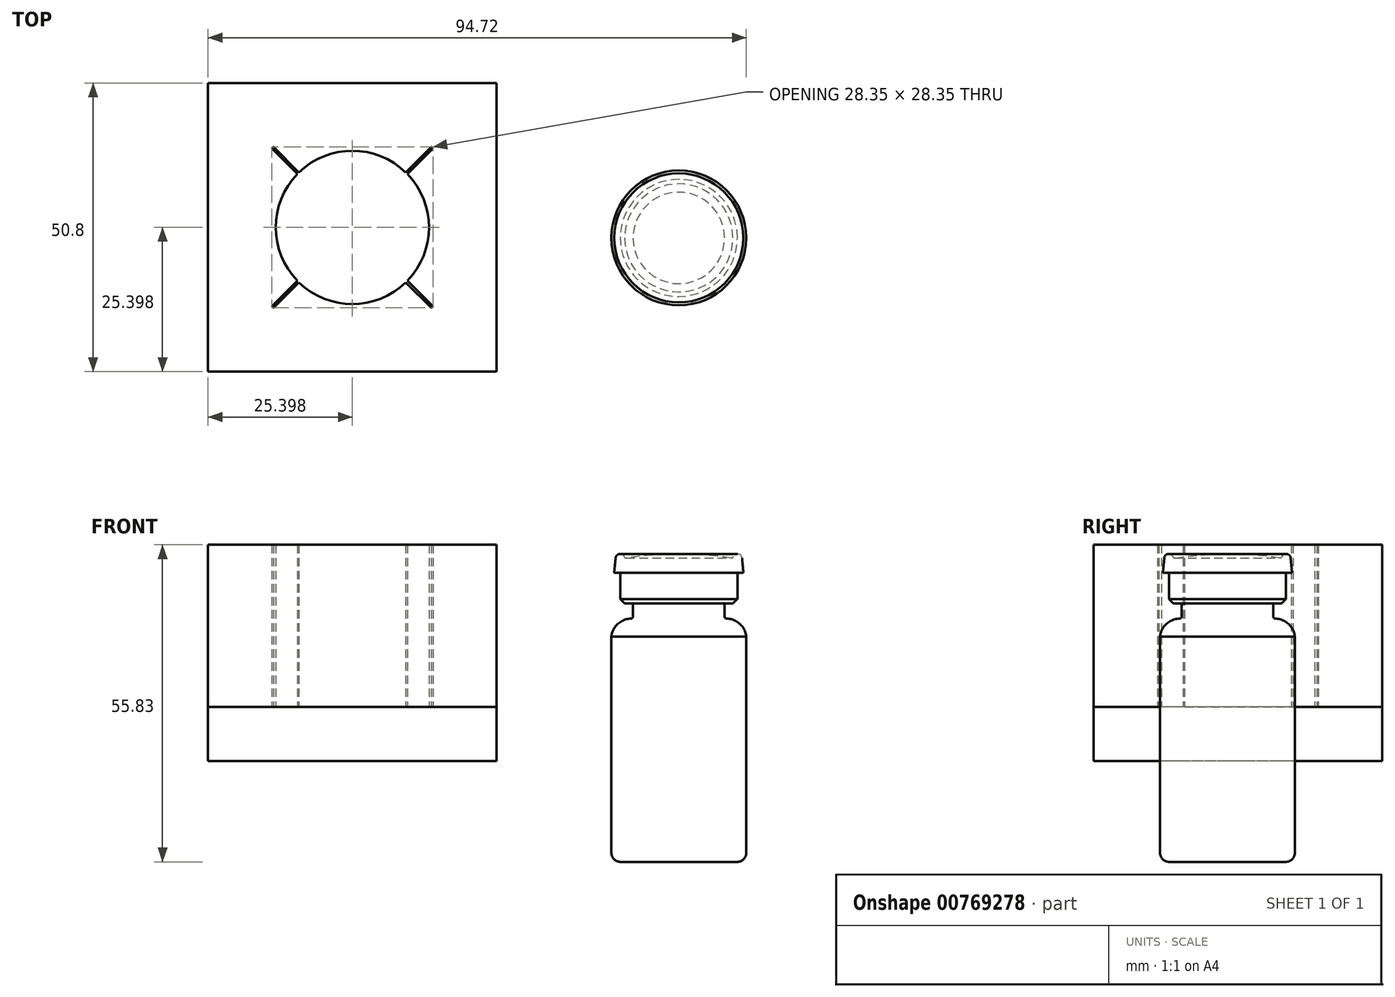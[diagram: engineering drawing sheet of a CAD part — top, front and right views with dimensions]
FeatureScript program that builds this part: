
annotation { "Feature Type Name" : "Feature", "Feature Type Description" : "" }
export const myFeature = defineFeature(function(context is Context, id is Id, definition is map)
    precondition{}
    {
        {
            var Q0;
            Q0=qCreatedBy(makeId("Top.planeOp"),FACE);
            var sketch = newSketch(context, id + "F0", { "sketchPlane" : qUnion([Q0])});
            skLineSegment(sketch, "E0", {"start": v(-12.56, 11.54) * mm, "end": v(-8.07, 16.03) * mm});
            skLineSegment(sketch, "E1", {"start": v(-12.28, 11.25) * mm, "end": v(-7.79, 15.75) * mm});
            skLineSegment(sketch, "E2", {"start": v(-12.28, -7.54) * mm, "end": v(-7.79, -12.03) * mm});
            skLineSegment(sketch, "E3", {"start": v(-12.56, -7.83) * mm, "end": v(-8.07, -12.32) * mm});
            skLineSegment(sketch, "E4", {"start": v(-35.85, -12.32) * mm, "end": v(-31.36, -7.83) * mm});
            skLineSegment(sketch, "E5", {"start": v(-36.14, -12.03) * mm, "end": v(-31.65, -7.54) * mm});
            skLineSegment(sketch, "E6", {"start": v(-36.14, 15.75) * mm, "end": v(-31.65, 11.25) * mm});
            skLineSegment(sketch, "E7", {"start": v(-35.85, 16.03) * mm, "end": v(-31.36, 11.54) * mm});
            skLineSegment(sketch, "E8", {"start": v(3.44, 27.26) * mm, "end": v(-47.36, 27.26) * mm});
            skLineSegment(sketch, "E9", {"start": v(3.44, 27.26) * mm, "end": v(3.44, -23.54) * mm});
            skLineSegment(sketch, "E10", {"start": v(3.44, -23.54) * mm, "end": v(-47.36, -23.54) * mm});
            skLineSegment(sketch, "E11", {"start": v(-47.36, 27.26) * mm, "end": v(-47.36, -23.54) * mm});
            skArc(sketch, "E12", {"start": v(-31.65, 11.25) * mm, "mid": v(-35.46, 1.86) * mm, "end": v(-31.65, -7.54) * mm});
            skArc(sketch, "E13", {"start": v(-31.36, -7.83) * mm, "mid": v(-21.96, -11.64) * mm, "end": v(-12.56, -7.83) * mm});
            skArc(sketch, "E14", {"start": v(-12.28, -7.54) * mm, "mid": v(-8.47, 1.86) * mm, "end": v(-12.28, 11.25) * mm});
            skArc(sketch, "E15", {"start": v(-12.56, 11.54) * mm, "mid": v(-21.96, 15.35) * mm, "end": v(-31.36, 11.54) * mm});
            skArc(sketch, "E16", {"start": v(-8.07, -12.32) * mm, "mid": v(-7.93, -12.17) * mm, "end": v(-7.79, -12.03) * mm});
            skArc(sketch, "E17", {"start": v(-7.79, 15.75) * mm, "mid": v(-7.93, 15.89) * mm, "end": v(-8.07, 16.03) * mm});
            skArc(sketch, "E18", {"start": v(-35.85, 16.03) * mm, "mid": v(-36, 15.89) * mm, "end": v(-36.14, 15.75) * mm});
            skArc(sketch, "E19", {"start": v(-36.14, -12.03) * mm, "mid": v(-36, -12.17) * mm, "end": v(-35.85, -12.32) * mm});
            skSolve(sketch);
        }
        {
            var Q0;
            Q0 = qSketchRegion(id + "F0", true);
            extrude(context, id + "F1", {"entities" : qUnion([Q0]), "depth" : 28.57 * mm, "offsetDistance" : 25.4 * mm});
        }
        {
            var Q0;
            Q0=makeQuery(id+"F1.opExtrude","CAP_FACE",FACE,{"disambiguationData":[OSD([sQuery(id+"F0.wireOp",EDGE,"E0"),sQuery(id+"F0.wireOp",EDGE,"E1"),sQuery(id+"F0.wireOp",EDGE,"E2"),sQuery(id+"F0.wireOp",EDGE,"E3"),sQuery(id+"F0.wireOp",EDGE,"E4"),sQuery(id+"F0.wireOp",EDGE,"E5"),sQuery(id+"F0.wireOp",EDGE,"E6"),sQuery(id+"F0.wireOp",EDGE,"E7"),sQuery(id+"F0.wireOp",EDGE,"E8"),sQuery(id+"F0.wireOp",EDGE,"E9"),sQuery(id+"F0.wireOp",EDGE,"E10"),sQuery(id+"F0.wireOp",EDGE,"E11"),sQuery(id+"F0.wireOp",EDGE,"E12"),sQuery(id+"F0.wireOp",EDGE,"E13"),sQuery(id+"F0.wireOp",EDGE,"E14"),sQuery(id+"F0.wireOp",EDGE,"E15"),sQuery(id+"F0.wireOp",EDGE,"E16"),sQuery(id+"F0.wireOp",EDGE,"E17"),sQuery(id+"F0.wireOp",EDGE,"E18"),sQuery(id+"F0.wireOp",EDGE,"E19")])],"isStart":true});
            var sketch = newSketch(context, id + "F2", { "sketchPlane" : qUnion([Q0])});
            skLineSegment(sketch, "E20.0", {"start": v(3.44, 23.54) * mm, "end": v(-47.36, 23.54) * mm});
            skLineSegment(sketch, "E20.1", {"start": v(3.44, -27.26) * mm, "end": v(3.44, 23.54) * mm});
            skLineSegment(sketch, "E20.2", {"start": v(3.44, -27.26) * mm, "end": v(-47.36, -27.26) * mm});
            skLineSegment(sketch, "E20.3", {"start": v(-47.36, -27.26) * mm, "end": v(-47.36, 23.54) * mm});
            skSolve(sketch);
        }
        {
            var Q0;
            Q0 = qSketchRegion(id + "F2", true);
            extrude(context, id + "F3", {"entities" : qUnion([Q0]), "depth" : 9.52 * mm, "offsetDistance" : 25.4 * mm});
        }
        {
            var Q0;
            Q0=qCreatedBy(makeId("Front.planeOp"),FACE);
            var sketch = newSketch(context, id + "F4", { "sketchPlane" : qUnion([Q0])});
            skLineSegment(sketch, "E21", {"start": v(35.5, -27.26) * mm, "end": v(45.77, -27.26) * mm});
            skArc(sketch, "E22", {"start": v(45.77, -27.26) * mm, "mid": v(46.9, -26.8) * mm, "end": v(47.36, -25.67) * mm});
            skLineSegment(sketch, "E23", {"start": v(47.36, -25.67) * mm, "end": v(47.36, 12.38) * mm});
            skArc(sketch, "E24", {"start": v(47.36, 12.38) * mm, "mid": v(46.26, 14.63) * mm, "end": v(43.93, 15.57) * mm});
            skArc(sketch, "E25", {"start": v(43.55, 15.96) * mm, "mid": v(43.66, 15.69) * mm, "end": v(43.93, 15.57) * mm});
            skLineSegment(sketch, "E26", {"start": v(46.85, 23.64) * mm, "end": v(45.8, 23.64) * mm});
            skLineSegment(sketch, "E27", {"start": v(45.01, 18.24) * mm, "end": v(43.55, 18.24) * mm});
            skLineSegment(sketch, "E28", {"start": v(43.55, 15.96) * mm, "end": v(43.55, 18.24) * mm});
            skLineSegment(sketch, "E29", {"start": v(45.8, 19.03) * mm, "end": v(45.8, 23.64) * mm});
            skLineSegment(sketch, "E30", {"start": v(45.8, 19.03) * mm, "end": v(45.01, 18.24) * mm});
            skLineSegment(sketch, "E31", {"start": v(46.85, 23.64) * mm, "end": v(46.63, 26.25) * mm});
            skArc(sketch, "E32", {"start": v(46.63, 26.25) * mm, "mid": v(45.95, 26.96) * mm, "end": v(45.1, 26.48) * mm});
            skArc(sketch, "E33", {"start": v(44.67, 26.24) * mm, "mid": v(44.93, 26.28) * mm, "end": v(45.1, 26.48) * mm});
            skArc(sketch, "E34", {"start": v(44.67, 26.24) * mm, "mid": v(40.1, 26.78) * mm, "end": v(35.5, 26.97) * mm});
            skLineSegment(sketch, "E35", {"start": v(35.5, 26.97) * mm, "end": v(35.5, -27.26) * mm});
            skSolve(sketch);
        }
        {
            var Q0;
            Q0 = qSketchRegion(id + "F4", true);
            var Q1;
            Q1=sQuery(id+"F4.wireOp",EDGE,"E35");
            revolve(context, id + "F5", {"surfaceOperationType" : NewSurfaceOperationType.NEW, "entities" : qUnion([Q0]), "axis" : qUnion([Q1]), "revolveType" : RevolveType.FULL});
        }
    });
